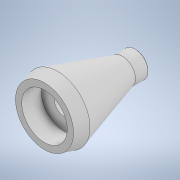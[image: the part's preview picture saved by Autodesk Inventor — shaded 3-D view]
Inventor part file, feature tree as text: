
AUTODESK INVENTOR PART (.ipt)
format: ipt  version: 2020 (Build 240168000, 168)  size: 130,560 bytes
history: native  units: in
note: dims shown in document units (in); Inventor stores cm internally (conversion verified against a paired STEP export)
features: sketch x4, extrude x2, plane x1, loft x1, hole x1, chamfer x1, other x1, projected_geometry x1
ambient origin geometry x8: Origin, YZ Plane, XZ Plane, XY Plane, X Axis, Y Axis, Z Axis, Center Point
bodies: Solid1 (feature_tree)
feature tree (12):
  extrude  "Extrusion1"  Depth=0.25in TaperAngle=0.0deg
  plane  "Work Plane1"
  loft  "Loft1"
  extrude  "Extrusion2"  TaperAngle=0.0deg  [1 undecoded]
  hole  "Hole1"  [1 undecoded]
  chamfer  "Chamfer1"  [1 undecoded]
  sketch  "Sketch1"  dims[d1=0.5in d2=0.25in d3=0.0in]
  sketch  "Sketch2"  dims[d4=1.25in d5=1.25in]
  other  "Edges1"
  sketch  "Sketch3"  dims[d6=0.0in d7=90.0deg d8=0.0in d9=90.0deg]
  projected_geometry  "Projected Loop1"
  sketch  "Sketch4"  dims[d10=0.25in d11=-0.1031in d12=0.375in d13=0.75in d14=0.875in d15=0.375in d16=0.5635in d17=1.0in d18=0.8108in d19=0.01in d20=0.125in d21=45.0deg]
note: 3 required parameter values undecoded (feature->parameter linkage not recoverable at this tier; creation-order binding heuristic only, values carry confidence <= 0.55)
